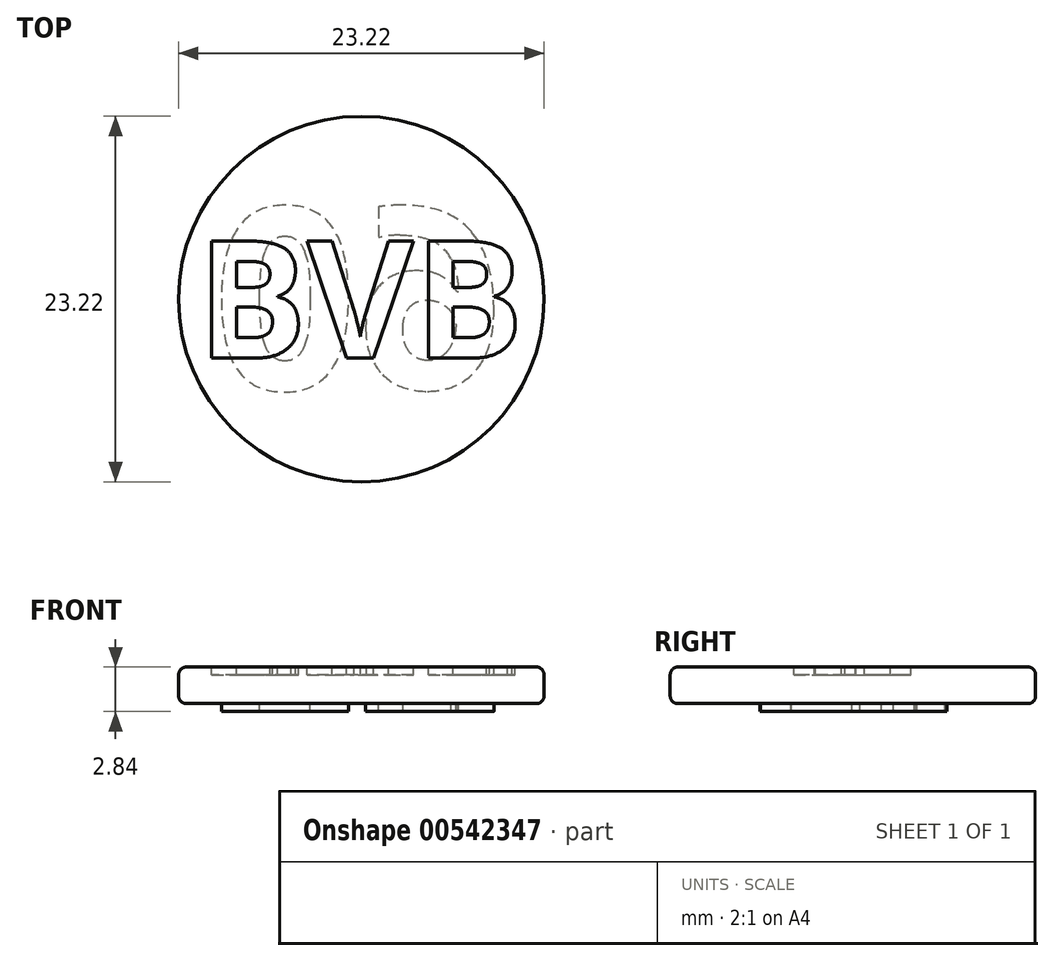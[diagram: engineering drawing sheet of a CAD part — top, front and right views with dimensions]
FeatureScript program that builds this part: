
annotation { "Feature Type Name" : "Feature", "Feature Type Description" : "" }
export const myFeature = defineFeature(function(context is Context, id is Id, definition is map)
    precondition{}
    {
        {
            var Q0;
            Q0=qCreatedBy(makeId("Top.planeOp"),FACE);
            var sketch = newSketch(context, id + "F0", { "sketchPlane" : qUnion([Q0])});
            skCircle(sketch, "E0", {"center": v(0, 0) * mm, "radius": 11.6 * mm});
            skSolve(sketch);
        }
        {
            var Q0;
            Q0=makeQuery(id+"F0.imprint","IMPRINT",FACE,{"disambiguationData":[TD([[makeQuery(id+"F0.imprint","IMPRINT",EDGE,{"derivedFrom":sQuery(id+"F0.wireOp",EDGE,"E0")}),1.0]])]});
            extrude(context, id + "F1", {"entities" : qUnion([Q0]), "endBound" : BoundingType.SYMMETRIC, "depth" : 2.33 * mm, "offsetDistance" : 25 * mm});
        }
        {
            var Q0;
            Q0=makeQuery(id+"F1.opExtrude","CAP_EDGE",EDGE,{"disambiguationData":[OSD([sQuery(id+"F0.wireOp",EDGE,"E0")])],"isStart":false});
            var Q1;
            Q1=makeQuery(id+"F1.opExtrude","CAP_EDGE",EDGE,{"disambiguationData":[OSD([sQuery(id+"F0.wireOp",EDGE,"E0")])],"isStart":true});
            fillet(context, id + "F2", {"entities" : qUnion([Q0, Q1]), "radius" : 0.5 * mm, "tangentPropagation" : true, "allowEdgeOverflow" : false});
        }
        {
            var Q0;
            Q0=makeQuery(id+"F1.opExtrude","CAP_FACE",FACE,{"disambiguationData":[OSD([sQuery(id+"F0.wireOp",EDGE,"E0")])],"isStart":false});
            var sketch = newSketch(context, id + "F3", { "sketchPlane" : qUnion([Q0])});
            skText(sketch, "E1", { "text": "BVB", "fontName": "OpenSans-Bold.ttf"});
            const initialGuessF3  = {"E1": [-0.01045, -0.00375, 1, 0, 0.0075]};
            skSetInitialGuess(sketch, initialGuessF3);
            skSolve(sketch);
        }
        {
            var Q0;
            Q0 = qSketchRegion(id + "F3", true);
            extrude(context, id + "F4", {"entities" : qUnion([Q0]), "operationType" : NewBodyOperationType.REMOVE, "oppositeDirection" : true, "depth" : 0.5 * mm, "offsetDistance" : 25 * mm});
        }
        {
            var Q0;
            Q0=makeQuery(id+"F1.opExtrude","CAP_FACE",FACE,{"disambiguationData":[OSD([sQuery(id+"F0.wireOp",EDGE,"E0")])],"isStart":true});
            var sketch = newSketch(context, id + "F5", { "sketchPlane" : qUnion([Q0])});
            skText(sketch, "E2", { "text": "09", "fontName": "OpenSans-Bold.ttf"});
            const initialGuessF5  = {"E2": [-0.00946, -0.00581, 1, 0, 0.01163]};
            skSetInitialGuess(sketch, initialGuessF5);
            skSolve(sketch);
        }
        {
            var Q0;
            Q0 = qSketchRegion(id + "F5", true);
            extrude(context, id + "F6", {"entities" : qUnion([Q0]), "operationType" : NewBodyOperationType.ADD, "depth" : 0.5 * mm, "offsetDistance" : 25 * mm});
        }
    });
